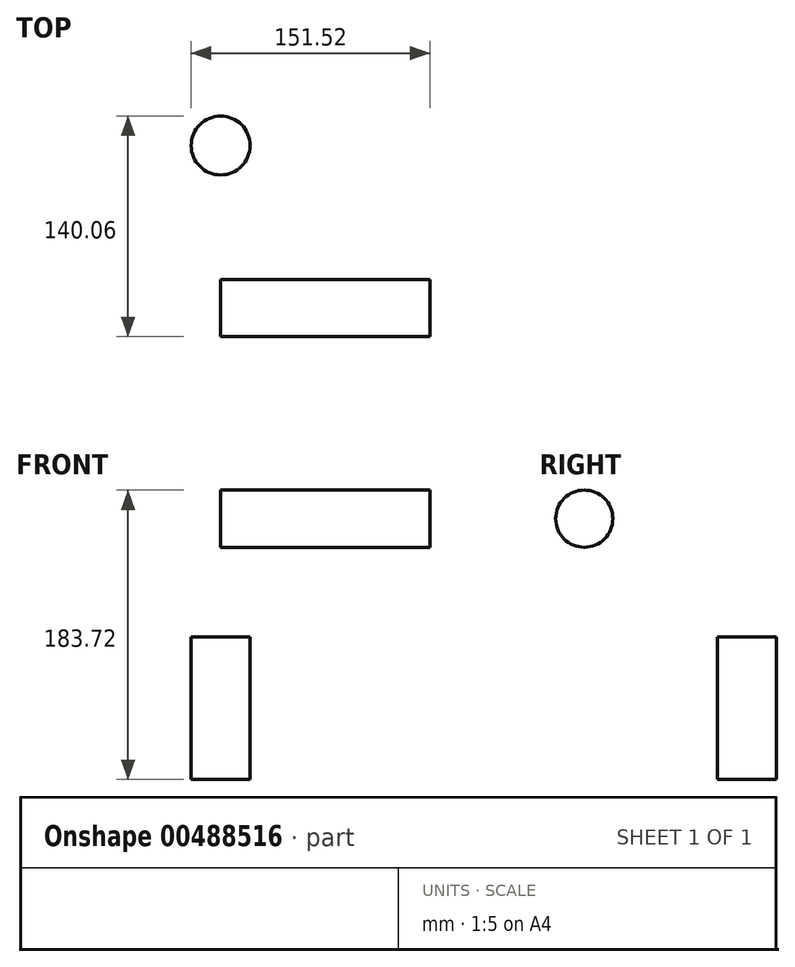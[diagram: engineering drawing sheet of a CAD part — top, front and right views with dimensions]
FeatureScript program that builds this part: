
annotation { "Feature Type Name" : "Feature", "Feature Type Description" : "" }
export const myFeature = defineFeature(function(context is Context, id is Id, definition is map)
    precondition{}
    {
        {
            var Q0;
            Q0=qCreatedBy(makeId("Top.planeOp"),FACE);
            var sketch = newSketch(context, id + "F0", { "sketchPlane" : qUnion([Q0])});
            skCircle(sketch, "E0", {"center": v(0, 0) * mm, "radius": 18.68 * mm});
            skSolve(sketch);
        }
        {
            var Q0;
            Q0 = qSketchRegion(id + "F0", true);
            extrude(context, id + "F1", {"entities" : qUnion([Q0]), "depth" : 90.42 * mm});
        }
        {
            var Q0;
            Q0=qCreatedBy(makeId("Right.planeOp"),FACE);
            var sketch = newSketch(context, id + "F2", { "sketchPlane" : qUnion([Q0])});
            skCircle(sketch, "E1", {"center": v(-103.24, 165.57) * mm, "radius": 18.15 * mm});
            skSolve(sketch);
        }
        {
            var Q0;
            Q0 = qSketchRegion(id + "F2", true);
            extrude(context, id + "F3", {"entities" : qUnion([Q0]), "depth" : 132.84 * mm});
        }
    });
